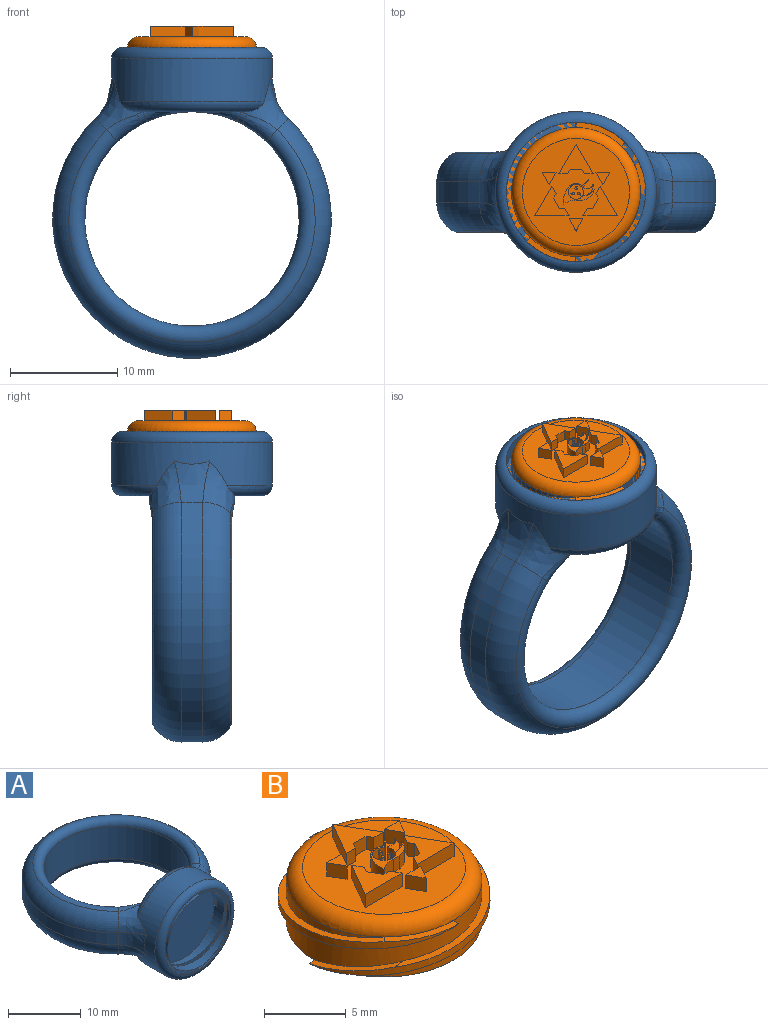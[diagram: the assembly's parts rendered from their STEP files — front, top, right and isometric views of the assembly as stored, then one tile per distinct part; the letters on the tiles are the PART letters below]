
ASSEMBLY  parts=2 mates=1
PART A: 46 faces, bbox 28.5x30.4x16.6 mm
  f0: cylinder r=6mm len=12mm, axis (0,1,0), area 43.6mm2, adj f1,f8,f9,f44,f45
  f1: plane 12x12mm, normal (0,1,0), area 113.1mm2, adj f0,f2
  f2: cylinder r=6mm len=12mm, axis (0,1,0), area 43.6mm2, adj f1,f3,f5,f6,f9
  f3: bspline ~13x11.1mm, area 12.3mm2, adj f2,f4,f5,f9
  f4: cylinder r=6.5mm len=13mm, axis (0,-1,0), area 14mm2, adj f3,f5,f8,f9
  f5: plane 0.5x0.5mm, normal (0,0,-1), area 0.3mm2, adj f2,f3,f4,f8
  f6: bspline ~13x13mm, area 14.8mm2, adj f2,f7,f9,f45
  f7: cylinder r=6.5mm len=13mm, axis (0,-1,0), area 14mm2, adj f6,f9,f44,f45
  f8: bspline ~13x13mm, area 14.8mm2, adj f0,f4,f5,f9
  f9: plane 13.01x13.01mm, normal (0,-1,0), area 250.8mm2, adj f0,f2,f3,f4,f6,f7,f8,f10
  f10: torus R=6.5mm, axis (0,-1,0), area 70.4mm2, adj f9,f11
  f11: cylinder r=7.5mm len=15mm, axis (0,1,0), area 165.8mm2, adj f10,f12,f37,f38,f39,f40,f41,f42
  f12: bspline ~8.06x5.54mm, area 11.7mm2, adj f11,f13,f34,f35,f36,f37,f43
  f13: plane 10.61x2.87mm, normal (0,1,0), area 17.9mm2, adj f12,f14,f32,f33,f34,f42,f43
  f14: plane 0.56x0.28mm, normal (0,0,1), area 0.1mm2, adj f13,f15,f42
  f15: torus R=11mm, axis (0,0,1), area 0.9mm2, adj f14,f16,f18,f32
  f16: bspline ~4.7x3.41mm, area 5.5mm2, adj f15,f17,f18,f42
  f17: torus R=11mm, axis (0,0,-1), area 105.4mm2, adj f16,f18,f35,f36
  f18: cylinder r=10mm len=20mm, axis (0,0,-1), area 358.6mm2, adj f15,f16,f17,f19,f20,f23,f24,f28
  f19: torus R=11mm, axis (0,0,1), area 0.9mm2, adj f18,f33,f34,f35
  f20: torus R=11mm, axis (0,0,-1), area 105.4mm2, adj f18,f21,f23,f31
  f21: torus R=10mm, axis (0,0,1), area 186.4mm2, adj f20,f22,f38,f40
  f22: cylinder r=13mm len=26mm, axis (0,0,-1), area 123.5mm2, adj f21,f36,f37,f41
  f23: bspline ~3.74x2.87mm, area 5.5mm2, adj f18,f20,f24,f38
  f24: torus R=11mm, axis (0,0,1), area 0.9mm2, adj f18,f23,f25,f28
  f25: plane 0.56x0.28mm, normal (0,0,-1), area 0.1mm2, adj f24,f26,f38
  f26: plane 10.61x2.87mm, normal (0,1,0), area 17.9mm2, adj f25,f27,f28,f29,f38,f39,f40
  f27: plane 0.56x0.28mm, normal (0,0,-1), area 0.1mm2, adj f26,f30,f40
  f28: bspline ~4.82x1.1mm, area 2.2mm2, adj f18,f24,f26
  f29: bspline ~4.82x1.1mm, area 2.2mm2, adj f18,f26,f30
  f30: torus R=11mm, axis (0,0,1), area 0.9mm2, adj f18,f27,f29,f31
  f31: bspline ~4.42x3.08mm, area 5.5mm2, adj f18,f20,f30,f40
  f32: bspline ~4.82x1.1mm, area 2.2mm2, adj f13,f15,f18
  f33: bspline ~4.82x1.1mm, area 2.2mm2, adj f13,f18,f19
  f34: plane 0.56x0.28mm, normal (0,0,1), area 0.1mm2, adj f12,f13,f19
  f35: bspline ~4.02x3.2mm, area 5.5mm2, adj f12,f17,f18,f19
  f36: torus R=10mm, axis (0,0,1), area 186.4mm2, adj f12,f17,f22,f42
  f37: bspline ~7.61x4.26mm, area 11.7mm2, adj f11,f12,f22,f38
  f38: bspline ~8.06x5.54mm, area 11.7mm2, adj f11,f21,f23,f25,f26,f37,f39
  f39: torus R=6.5mm, axis (0,-1,0), area 22.8mm2, adj f11,f26,f38,f40
  f40: bspline ~7.6x5.54mm, area 11.7mm2, adj f11,f21,f26,f27,f31,f39,f41
  f41: bspline ~7.61x4.26mm, area 11.7mm2, adj f11,f22,f40,f42
  f42: bspline ~7.6x5.54mm, area 11.7mm2, adj f11,f13,f14,f16,f36,f41,f43
  f43: torus R=6.5mm, axis (0,-1,0), area 22.8mm2, adj f11,f12,f13,f42
  f44: bspline ~13x11.1mm, area 12.3mm2, adj f0,f7,f9,f45
  f45: plane 0.5x0.5mm, normal (0,0,1), area 0.3mm2, adj f0,f6,f7,f44
PART B: 81 faces, bbox 13.4x13x5 mm
  f0: cylinder r=6.5mm len=13mm, axis (0,0,1), area 12.7mm2, adj f1,f72,f73,f78,f79
  f1: bspline ~11.1x11.1mm, area 9.4mm2, adj f0,f4,f78,f79
  f2: bspline ~11.09x11.09mm, area 9.4mm2, adj f3,f5,f76,f80
  f3: cylinder r=6.5mm len=13mm, axis (0,0,1), area 12.7mm2, adj f2,f74,f75,f76,f80
  f4: cylinder r=6mm len=12mm, axis (0,0,-1), area 44.9mm2, adj f1,f7,f8,f72,f75,f79
  f5: cylinder r=6mm len=12mm, axis (0,0,-1), area 45mm2, adj f2,f7,f8,f73,f74,f80
  f6: plane 10x10mm, normal (0,0,1), area 62.9mm2, adj f8,f9,f10,f11,f12,f13,f14,f15
  f7: plane 12x12mm, normal (0,0,-1), area 113.1mm2, adj f4,f5
  f8: torus R=5mm, axis (0,0,1), area 55.4mm2, adj f4,f5,f6,f77,f78
  f9: plane 2.77x1.6mm, normal (0.87,0.5,0), area 3.2mm2, adj f6,f10,f15,f16
  f10: plane 2.77x1.6mm, normal (-0.87,0.5,0), area 3.2mm2, adj f6,f9,f11,f16
  f11: plane 1x0.8mm, normal (0,-1,0), area 0.8mm2, adj f6,f10,f12,f16
  f12: plane 1x0.43mm, normal (0.87,-0.5,0), area 0.5mm2, adj f6,f11,f13,f16
  f13: plane 1.1x1mm, normal (0,-1,0), area 1.1mm2, adj f6,f12,f14,f16
  f14: plane 1x0.43mm, normal (-0.87,-0.5,0), area 0.5mm2, adj f6,f13,f15,f16
  f15: plane 1x0.8mm, normal (0,-1,0), area 0.8mm2, adj f6,f9,f14,f16
  f16: plane 3.2x2.77mm, normal (0,0,1), area 3.8mm2, adj f9,f10,f11,f12,f13,f14,f15
  f17: plane 2.77x1.6mm, normal (0.87,0.5,0), area 3.2mm2, adj f6,f18,f23,f24
  f18: plane 1x0.69mm, normal (-0.87,0.5,0), area 0.8mm2, adj f6,f17,f19,f24
  f19: plane 1x0.43mm, normal (-0.87,-0.5,0), area 0.5mm2, adj f6,f18,f20,f24
  f20: plane 1x0.95mm, normal (-0.87,0.5,0), area 1.1mm2, adj f6,f19,f21,f24
  f21: plane 1x0.5mm, normal (0,1,0), area 0.5mm2, adj f6,f20,f22,f24
  f22: plane 1x0.69mm, normal (-0.87,0.5,0), area 0.8mm2, adj f6,f21,f23,f24
  f23: plane 3.2x1mm, normal (0,-1,0), area 3.2mm2, adj f6,f17,f22,f24
  f24: plane 3.2x2.77mm, normal (0,0,1), area 3.8mm2, adj f17,f18,f19,f20,f21,f22,f23
  f25: plane 3.2x1mm, normal (0,-1,0), area 3.2mm2, adj f6,f26,f31,f32
  f26: plane 1x0.69mm, normal (0.87,0.5,0), area 0.8mm2, adj f6,f25,f27,f32
  f27: plane 1x0.5mm, normal (0,1,0), area 0.5mm2, adj f6,f26,f28,f32
  f28: plane 1x0.95mm, normal (0.87,0.5,0), area 1.1mm2, adj f6,f27,f29,f32
  f29: plane 1x0.43mm, normal (0.87,-0.5,0), area 0.5mm2, adj f6,f28,f30,f32
  f30: plane 1x0.69mm, normal (0.87,0.5,0), area 0.8mm2, adj f6,f29,f31,f32
  f31: plane 2.77x1.6mm, normal (-0.87,0.5,0), area 3.2mm2, adj f6,f25,f30,f32
  f32: plane 3.2x2.77mm, normal (0,0,1), area 3.8mm2, adj f25,f26,f27,f28,f29,f30,f31
  f33: plane 1.13x1mm, normal (0.87,-0.5,0), area 1.3mm2, adj f6,f34,f35,f36
  f34: plane 1.3x1mm, normal (0,1,0), area 1.3mm2, adj f6,f33,f35,f36
  f35: plane 1.13x1mm, normal (-0.87,-0.5,0), area 1.3mm2, adj f6,f33,f34,f36
  f36: plane 1.3x1.13mm, normal (0,0,1), area 0.7mm2, adj f33,f34,f35
  f37: plane 1.13x1mm, normal (-0.87,-0.5,0), area 1.3mm2, adj f6,f38,f39,f40
  f38: plane 1.13x1mm, normal (0.87,-0.5,0), area 1.3mm2, adj f6,f37,f39,f40
  f39: plane 1.3x1mm, normal (0,1,0), area 1.3mm2, adj f6,f37,f38,f40
  f40: plane 1.3x1.13mm, normal (0,0,1), area 0.7mm2, adj f37,f38,f39
  f41: plane 1.3x1mm, normal (0,1,0), area 1.3mm2, adj f6,f42,f43,f44
  f42: plane 1.13x1mm, normal (-0.87,-0.5,0), area 1.3mm2, adj f6,f41,f43,f44
  f43: plane 1.13x1mm, normal (0.87,-0.5,0), area 1.3mm2, adj f6,f41,f42,f44
  f44: plane 1.3x1.13mm, normal (0,0,1), area 0.7mm2, adj f41,f42,f43
  f45: cylinder r=1.6mm len=1.13mm, axis (0,0,-1), area 1.2mm2, adj f6,f46,f58,f59
  f46: plane 1x0.5mm, normal (0,-1,0), area 0.5mm2, adj f6,f45,f47,f59
  f47: cylinder r=1.3mm len=1.19mm, axis (0,0,-1), area 1.7mm2, adj f6,f46,f48,f59
  f48: cylinder r=1mm len=1mm, axis (0,0,-1), area 1.2mm2, adj f6,f47,f49,f59
  f49: cylinder r=1mm len=1.05mm, axis (0,0,-1), area 1.5mm2, adj f6,f48,f50,f59
  f50: cylinder r=0.5mm len=1mm, axis (0,0,-1), area 0.7mm2, adj f6,f49,f51,f59
  f51: cylinder r=1.27mm len=1mm, axis (0,0,-1), area 0.4mm2, adj f6,f50,f52,f59
  f52: plane 1x0.07mm, normal (-0.71,0.71,0), area 0.1mm2, adj f6,f51,f53,f59
  f53: cylinder r=0.7mm len=1.4mm, axis (0,0,-1), area 4.3mm2, adj f6,f52,f54,f59
  f54: plane 1x0.64mm, normal (0.71,-0.71,0), area 0.9mm2, adj f6,f53,f55,f59
  f55: plane 1x0.07mm, normal (0.71,0.71,0), area 0.1mm2, adj f6,f54,f56,f59
  f56: plane 1x0.57mm, normal (-0.71,0.71,0), area 0.8mm2, adj f6,f55,f57,f59
  f57: cylinder r=0.8mm len=1.13mm, axis (0,0,-1), area 1.3mm2, adj f6,f56,f58,f59
  f58: cylinder r=1.9mm len=1.7mm, axis (0,0,-1), area 1.9mm2, adj f6,f45,f57,f59
  f59: plane 2.85x2.26mm, normal (0,0,1), area 1.8mm2, adj f45,f46,f47,f48,f49,f50,f51,f52
  f60: cylinder r=0.1mm len=1mm, axis (0,0,-1), area 0.5mm2, adj f6,f61,f62,f63
  f61: cylinder r=0.2mm len=1mm, axis (0,0,-1), area 0.1mm2, adj f6,f60,f62,f63
  f62: cylinder r=0.2mm len=1mm, axis (0,0,-1), area 0.3mm2, adj f6,f60,f61,f63
  f63: plane 0.29x0.25mm, normal (0,0,1), area 0mm2, adj f60,f61,f62
  f64: cylinder r=0.1mm len=1mm, axis (0,0,-1), area 0.5mm2, adj f6,f65,f66,f67
  f65: cylinder r=0.2mm len=1mm, axis (0,0,-1), area 0.1mm2, adj f6,f64,f66,f67
  f66: cylinder r=0.2mm len=1mm, axis (0,0,-1), area 0.3mm2, adj f6,f64,f65,f67
  f67: plane 0.3x0.2mm, normal (0,0,1), area 0mm2, adj f64,f65,f66
  f68: cylinder r=0.1mm len=1mm, axis (0,0,-1), area 0.5mm2, adj f6,f69,f70,f71
  f69: cylinder r=0.2mm len=1mm, axis (0,0,-1), area 0.1mm2, adj f6,f68,f70,f71
  f70: cylinder r=0.2mm len=1mm, axis (0,0,-1), area 0.3mm2, adj f6,f68,f69,f71
  f71: plane 0.32x0.21mm, normal (0,0,1), area 0mm2, adj f68,f69,f70
  f72: plane 0.5x0.04mm, normal (0,-1,0), area 0mm2, adj f0,f4,f73,f79
  f73: bspline ~13x13mm, area 14.8mm2, adj f0,f5,f72,f78
  f74: plane 0.5x0.04mm, normal (0,1,0), area 0mm2, adj f3,f5,f75,f80
  f75: bspline ~13x13mm, area 14.8mm2, adj f3,f4,f74,f76
  f76: plane 4.6x2.26mm, normal (0,0,1), area 2.5mm2, adj f2,f3,f75,f77
  f77: cylinder r=6mm len=4.24mm, axis (0,0,-1), area 0.2mm2, adj f8,f76
  f78: plane 4.6x2.26mm, normal (0,0,1), area 2.5mm2, adj f0,f1,f8,f73
  f79: bspline ~5.01x3.65mm, area 3mm2, adj f0,f1,f4,f72
  f80: bspline ~5.01x3.65mm, area 3mm2, adj f2,f3,f5,f74
PLACE A rot(axis=(-1,0,0),90deg) t=(-1.91,0.29,-13.24)mm
PLACE B t=(-1.91,0.29,-0.24)mm
MATE fastened A.f0 <-> B.f0  axis (0,0,1) through (-1.91,0.29,-0.24)mm
